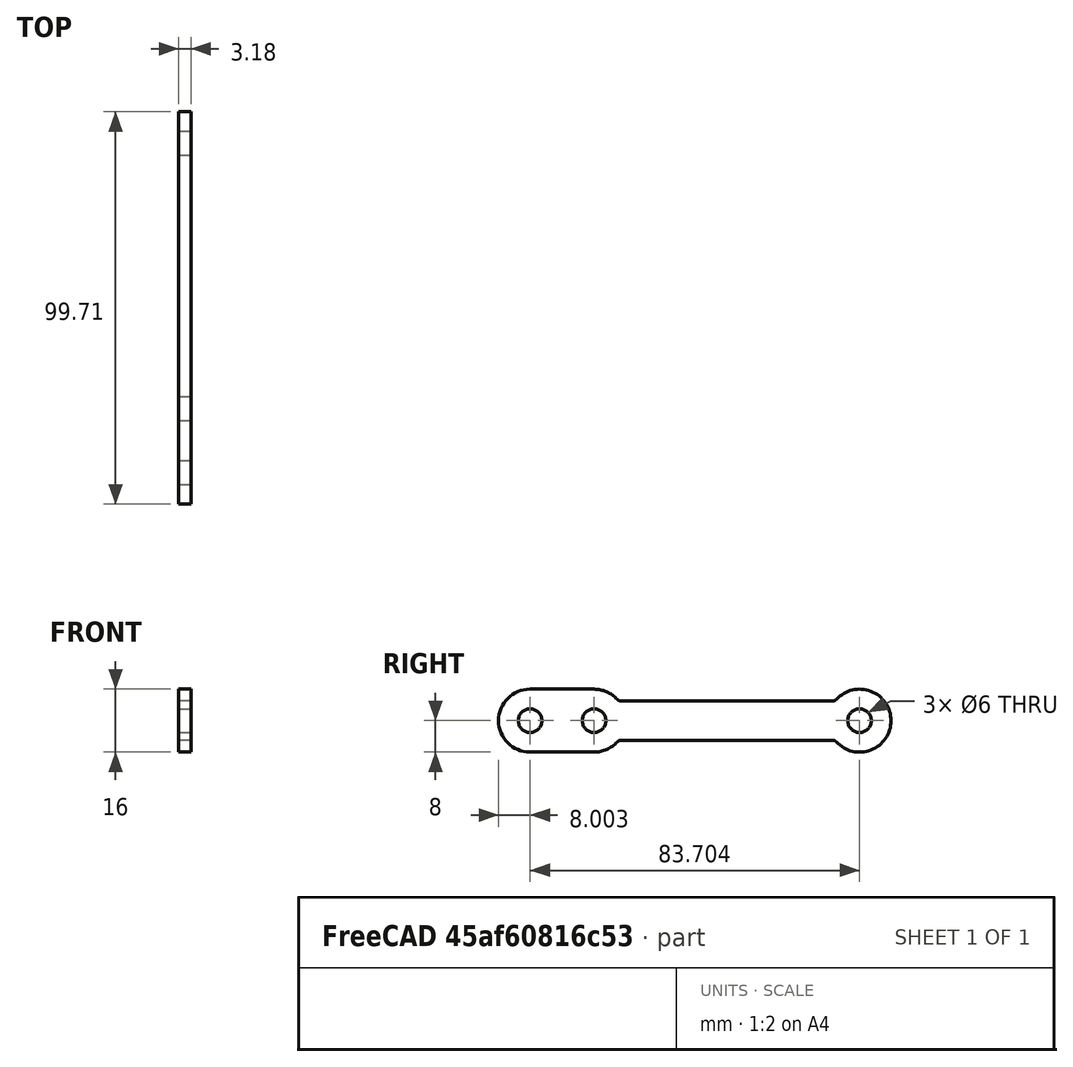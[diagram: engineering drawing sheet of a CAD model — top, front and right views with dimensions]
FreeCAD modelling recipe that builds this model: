
FCSTD DOCUMENT  (FreeCAD 1.0R38641 +468 (Git))
Label: frame_panel_spacer
License: All rights reserved
LicenseURL: https://en.wikipedia.org/wiki/All_rights_reserved
objects: PartDesign::SubShapeBinder×2, Sketcher::SketchObject×1, PartDesign::Pad×1, PartDesign::Body×1
note: 8 computed .brp shape members not serialized (recipe doc carries the construction recipe); baked Part::Feature solids carry a one-line shape summary decoded from their .brp
EXTERNAL_REF file=panel_side.FCStd obj=Body001
EXTERNAL_REF file=dimensions.FCStd obj=VarSet
EXTERNAL_REF file=frame_bracket.FCStd obj=Body

FEATURE [PartDesign::SubShapeBinder] Binder  label="SidePanelBinder"
  BindCopyOnChange = 0
  BindMode = 0
  ClaimChildren = false
  Context = -> Body [Binder.]
  Fuse = false
  MakeFace = true
  OffsetFill = false
  OffsetIntersection = false
  OffsetJoinType = 0
  OffsetOpenResult = false
  PartialLoad = false
  Refine = true
  Relative = true
  Support = -> [<external panel_side.FCStd>#Body001]
  _Version = 2
FEATURE [PartDesign::SubShapeBinder] Binder001  label="BracketBinder"
  BindCopyOnChange = 0
  BindMode = 0
  ClaimChildren = false
  Context = -> Body [Binder001.]
  Fuse = false
  MakeFace = true
  OffsetFill = false
  OffsetIntersection = false
  OffsetJoinType = 0
  OffsetOpenResult = false
  PartialLoad = false
  Refine = true
  Relative = true
  Support = -> [<external frame_bracket.FCStd>#Body]
  _Version = 2
FEATURE [Sketcher::SketchObject] Sketch
  ArcFitTolerance = 1e-06
  AttachmentSupport = -> [Binder]
  ExternalGeometry = -> [Binder,Binder001]
  FullyConstrained = true
  MakeInternals = false
  MapMode = 5
  Placement = pos=(-1.8542,0,0) rot=(0.57735,0.57735,0.57735;2.0944rad)
  expr: Constraints[32] = dimensions#VarSet.FrameMinWidth
  expr: Constraints[33] = dimensions#VarSet.EnclosureCornerRadius
  expr: Constraints[41] = dimensions#VarSet.FrameHoleDiameter
  expr: Constraints[42] = dimensions#VarSet.FrameHoleDiameter / 2 + dimensions#VarSet.FrameMinWidth / 2
  sketch-geometry (21):
    g0: ArcOfCircle CenterX=56.923 CenterY=-56.25 CenterZ=0 NormalX=0 NormalY=0 NormalZ=1 AngleXU=0 Radius=8 StartAngle=1.5708 EndAngle=4.71239
    g1: ArcOfCircle CenterX=73.177 CenterY=-56.25 CenterZ=0 NormalX=0 NormalY=0 NormalZ=1 AngleXU=0 Radius=8 StartAngle=0.739492 EndAngle=1.5708
    g2: ArcOfCircle CenterX=79.9741 CenterY=-50.05 CenterZ=0 NormalX=0 NormalY=0 NormalZ=1 AngleXU=0 Radius=1.2 StartAngle=3.88109 EndAngle=4.71239
    g3: ArcOfCircle CenterX=73.177 CenterY=-56.25 CenterZ=0 NormalX=0 NormalY=0 NormalZ=1 AngleXU=0 Radius=8 StartAngle=4.71239 EndAngle=5.54369
    g4: ArcOfCircle CenterX=79.9741 CenterY=-62.45 CenterZ=0 NormalX=0 NormalY=0 NormalZ=1 AngleXU=0 Radius=1.2 StartAngle=1.5708 EndAngle=2.4021
    g5: ArcOfCircle CenterX=140.627 CenterY=-56.25 CenterZ=0 NormalX=0 NormalY=0 NormalZ=1 AngleXU=0 Radius=8 StartAngle=3.88109 EndAngle=8.68529
    g6: ArcOfCircle CenterX=133.83 CenterY=-62.45 CenterZ=0 NormalX=0 NormalY=0 NormalZ=1 AngleXU=0 Radius=1.2 StartAngle=0.739492 EndAngle=1.5708
    g7: ArcOfCircle CenterX=133.83 CenterY=-50.05 CenterZ=0 NormalX=0 NormalY=0 NormalZ=1 AngleXU=0 Radius=1.2 StartAngle=4.71239 EndAngle=5.54369
    g8: LineSegment StartX=56.923 StartY=-48.25 StartZ=0 EndX=73.177 EndY=-48.25 EndZ=0
    g9: LineSegment StartX=56.923 StartY=-64.25 StartZ=0 EndX=73.177 EndY=-64.25 EndZ=0
    g10: LineSegment StartX=79.9741 StartY=-61.25 StartZ=0 EndX=133.83 EndY=-61.25 EndZ=0
    g11: LineSegment StartX=79.9741 StartY=-51.25 StartZ=0 EndX=133.83 EndY=-51.25 EndZ=0
    g12: LineSegment [constr] StartX=56.923 StartY=-56.25 StartZ=0 EndX=140.627 EndY=-56.25 EndZ=0
    g13: LineSegment [constr] StartX=56.923 StartY=-48.25 StartZ=0 EndX=56.923 EndY=-64.25 EndZ=0
    g14: LineSegment [constr] StartX=73.177 StartY=-48.25 StartZ=0 EndX=73.177 EndY=-64.25 EndZ=0
    g15: Circle CenterX=56.923 CenterY=-56.25 CenterZ=0 NormalX=0 NormalY=0 NormalZ=1 AngleXU=0 Radius=3
    g16: Circle CenterX=73.177 CenterY=-56.25 CenterZ=0 NormalX=0 NormalY=0 NormalZ=1 AngleXU=0 Radius=3
    g17: Circle CenterX=140.627 CenterY=-56.25 CenterZ=0 NormalX=0 NormalY=0 NormalZ=1 AngleXU=0 Radius=3
    g18: LineSegment [constr] StartX=148.627 StartY=-123.7 StartZ=0 EndX=148.627 EndY=-56.25 EndZ=0
    g19: Circle [constr] CenterX=56.923 CenterY=-56.25 CenterZ=0 NormalX=0 NormalY=0 NormalZ=1 AngleXU=0 Radius=8
    g20: Circle [constr] CenterX=73.177 CenterY=-56.25 CenterZ=0 NormalX=0 NormalY=0 NormalZ=1 AngleXU=0 Radius=8
  constraints (51):
    c: Coincident(g3,g1)
    c: Coincident(g8,g0)
    c: Coincident(g8,g1)
    c: Horizontal(g8)
    c: Coincident(g9,g0)
    c: Coincident(g9,g3)
    c: Horizontal(g9)
    c: Horizontal(g11)
    c: Horizontal(g10)
    c: Tangent(g4,g3) = 1.5708
    c: Tangent(g2,g1) = 1.5708
    c: Tangent(g7,g5) = 1.5708
    c: Tangent(g5,g6) = 1.5708
    c: Coincident(g12,g0)
    c: Coincident(g12,g5)
    c: Horizontal(g12)
    c: Coincident(g13,g0)
    c: Coincident(g13,g0)
    c: Vertical(g13)
    c: PointOnObject(g0,g13)
    c: Coincident(g14,g1)
    c: Coincident(g14,g3)
    c: PointOnObject(g1,g14)
    c: Vertical(g14)
    c: Tangent(g11,g2) = -1.5708
    c: Tangent(g10,g4) = 1.5708
    c: Tangent(g7,g11) = -1.5708
    c: Tangent(g10,g6) = 1.5708
    c: Equal(g1,g5)
    c: Equal(g2,g7)
    c: Equal(g6,g4)
    c: Symmetric(g4,g2,g12)
    c: Distance(g10,g11) = 10
    c: Radius(g2) = 1.2
    c: Coincident(g0,g-3)
    c: Coincident(g1,g-4)
    c: Coincident(g15,g0)
    c: Coincident(g16,g1)
    c: Coincident(g17,g5)
    c: Equal(g17,g16)
    c: Equal(g16,g15)
    c: Diameter(g15) = 6
    c: Radius(g0) = 8
    c: Vertical(g18)
    c: Coincident(g-5,g18)
    c: Tangent(g18,g5) = -1.5708
    c: Coincident(g19,g0)
    c: Equal(g19,g0)
    c: Coincident(g20,g1)
    c: Equal(g20,g1)
    c: Distance(g19,g20) = 0.254
FEATURE [PartDesign::Pad] Pad
  Direction = (1,0,0)
  Length = 3.175
  Length2 = 10
  Profile = -> Sketch
  ReferenceAxis = -> Sketch [N_Axis]
  Refine = true
  Reversed = true
  Suppressed = false
  Type = 0
  expr: Length = <<dimensions>>#VarSet.FrameTotalThickness
FEATURE [PartDesign::Body] Body  label="FramePanelSpacer"
  AllowCompound = false
  Group = -> [Pad,Sketch,Binder,Binder001]
  Origin = -> Origin
  Tip = -> Pad
